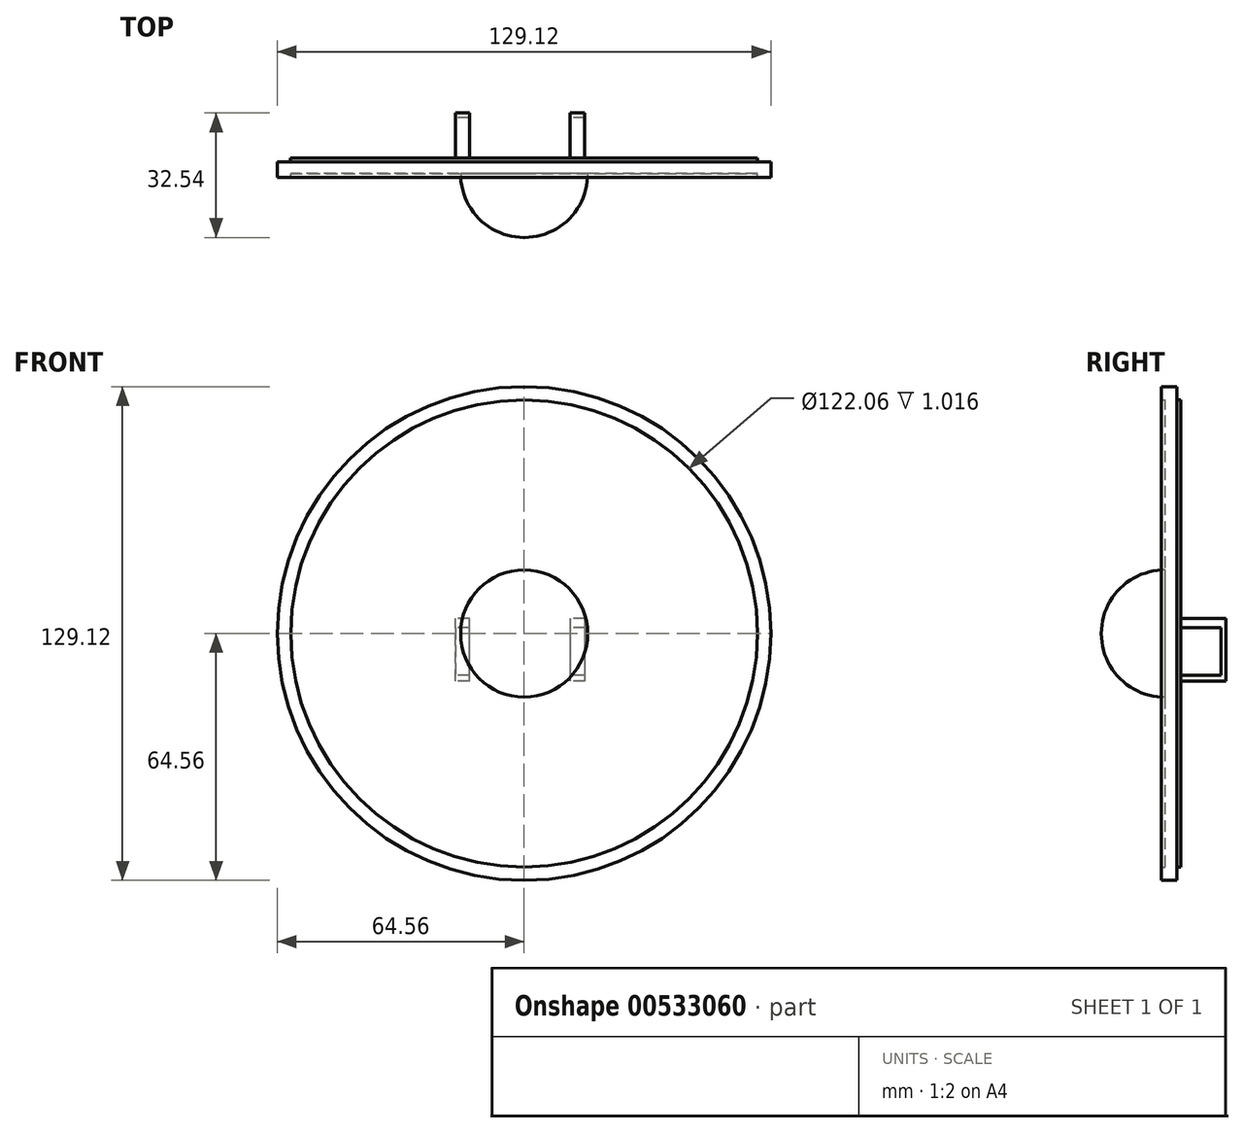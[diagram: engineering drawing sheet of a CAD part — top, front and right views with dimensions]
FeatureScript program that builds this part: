
annotation { "Feature Type Name" : "Feature", "Feature Type Description" : "" }
export const myFeature = defineFeature(function(context is Context, id is Id, definition is map)
    precondition{}
    {
        {
            var Q0;
            Q0=qCreatedBy(makeId("Front.planeOp"),FACE);
            var sketch = newSketch(context, id + "F0", { "sketchPlane" : qUnion([Q0])});
            skCircle(sketch, "E0", {"center": v(0, 0) * mm, "radius": 64.56 * mm});
            skSolve(sketch);
        }
        {
            var Q0;
            Q0=makeQuery(id+"F0.imprint","IMPRINT",FACE,{"disambiguationData":[TD([[makeQuery(id+"F0.imprint","IMPRINT",EDGE,{"derivedFrom":sQuery(id+"F0.wireOp",EDGE,"E0")}),1.0]])]});
            extrude(context, id + "F1", {"entities" : qUnion([Q0]), "endBound" : BoundingType.SYMMETRIC, "depth" : 3.05 * mm, "offsetDistance" : 25.4 * mm});
        }
        {
            var Q0;
            Q0=makeQuery(id+"F1.opExtrude","CAP_FACE",FACE,{"disambiguationData":[OSD([sQuery(id+"F0.wireOp",EDGE,"E0")])],"isStart":false});
            var sketch = newSketch(context, id + "F2", { "sketchPlane" : qUnion([Q0])});
            skCircle(sketch, "E1", {"center": v(0, 0) * mm, "radius": 61.03 * mm});
            skSolve(sketch);
        }
        {
            var Q0;
            Q0=makeQuery(id+"F2.imprint","IMPRINT",FACE,{"disambiguationData":[TD([[makeQuery(id+"F2.imprint","IMPRINT",EDGE,{"derivedFrom":sQuery(id+"F2.wireOp",EDGE,"E1")}),-1.0]])]});
            extrude(context, id + "F3", {"entities" : qUnion([Q0]), "operationType" : NewBodyOperationType.ADD, "depth" : 1.02 * mm, "offsetDistance" : 25.4 * mm});
        }
        {
            var Q0;
            Q0=makeQuery(id+"F1.opExtrude","CAP_FACE",FACE,{"disambiguationData":[OSD([sQuery(id+"F0.wireOp",EDGE,"E0")])],"isStart":false});
            var sketch = newSketch(context, id + "F4", { "sketchPlane" : qUnion([Q0])});
            skCircle(sketch, "E2", {"center": v(0, 0) * mm, "radius": 16.62 * mm});
            skSolve(sketch);
        }
        {
            var Q0;
            Q0=makeQuery(id+"F4.imprint","IMPRINT",FACE,{"disambiguationData":[TD([[makeQuery(id+"F4.imprint","IMPRINT",EDGE,{"derivedFrom":sQuery(id+"F4.wireOp",EDGE,"E2")}),1.0]])]});
            extrude(context, id + "F5", {"entities" : qUnion([Q0]), "operationType" : NewBodyOperationType.ADD, "depth" : 16.76 * mm, "offsetDistance" : 25.4 * mm});
        }
        {
            var Q0;
            Q0=makeQuery(id+"F5.opExtrude","CAP_EDGE",EDGE,{"disambiguationData":[OSD([sQuery(id+"F4.wireOp",EDGE,"E2")])],"isStart":false});
            fillet(context, id + "F6", {"entities" : qUnion([Q0]), "radius" : 16.56 * mm, "tangentPropagation" : true, "allowEdgeOverflow" : false});
        }
        {
            var Q0;
            Q0=makeQuery(id+"F1.opExtrude","CAP_FACE",FACE,{"disambiguationData":[OSD([sQuery(id+"F0.wireOp",EDGE,"E0")])],"isStart":true});
            var sketch = newSketch(context, id + "F7", { "sketchPlane" : qUnion([Q0])});
            skCircle(sketch, "E3", {"center": v(0, 0) * mm, "radius": 61.09 * mm});
            skSolve(sketch);
        }
        {
            var Q0;
            Q0 = qSketchRegion(id + "F7", true);
            extrude(context, id + "F8", {"entities" : qUnion([Q0]), "operationType" : NewBodyOperationType.ADD, "depth" : 1.02 * mm, "offsetDistance" : 25.4 * mm});
        }
        {
            var Q0;
            Q0=makeQuery(id+"F1.opExtrude","CAP_FACE",FACE,{"disambiguationData":[OSD([sQuery(id+"F0.wireOp",EDGE,"E0")])],"isStart":false});
            var sketch = newSketch(context, id + "F9", { "sketchPlane" : qUnion([Q0])});
            skLineSegment(sketch, "E4", {"start": v(-51.1, 33.39) * mm, "end": v(-51.1, -33.39) * mm});
            skLineSegment(sketch, "E5", {"start": v(-39.3, 46.7) * mm, "end": v(-39.3, -46.7) * mm});
            skLineSegment(sketch, "E6", {"start": v(-24.4, -55.94) * mm, "end": v(-24.4, 55.94) * mm});
            skLineSegment(sketch, "E7", {"start": v(-11.26, 59.99) * mm, "end": v(-11.26, 12.23) * mm});
            skLineSegment(sketch, "E8", {"start": v(-10.94, -12.5) * mm, "end": v(-10.94, -60.04) * mm});
            skLineSegment(sketch, "E9", {"start": v(3.47, -16.25) * mm, "end": v(3.47, -60.93) * mm});
            skLineSegment(sketch, "E10", {"start": v(3.1, 16.33) * mm, "end": v(3.1, 60.95) * mm});
            skLineSegment(sketch, "E11", {"start": v(17.62, 58.43) * mm, "end": v(17.62, -58.43) * mm});
            skLineSegment(sketch, "E12", {"start": v(32.37, -51.74) * mm, "end": v(32.37, 51.74) * mm});
            skLineSegment(sketch, "E13", {"start": v(48.38, -37.2) * mm, "end": v(48.38, 37.2) * mm});
            skSolve(sketch);
        }
        {
            var Q0;
            Q0=sQuery(id+"F9.wireOp",EDGE,"E4");
            var Q1;
            Q1=sQuery(id+"F9.wireOp",EDGE,"E5");
            var Q2;
            Q2=sQuery(id+"F9.wireOp",EDGE,"E6");
            var Q3;
            Q3=sQuery(id+"F9.wireOp",EDGE,"E7");
            var Q4;
            Q4=sQuery(id+"F9.wireOp",EDGE,"E8");
            var Q5;
            Q5=sQuery(id+"F9.wireOp",EDGE,"E10");
            var Q6;
            Q6=sQuery(id+"F9.wireOp",EDGE,"E9");
            var Q7;
            Q7=sQuery(id+"F9.wireOp",EDGE,"E11");
            var Q8;
            Q8=sQuery(id+"F9.wireOp",EDGE,"E12");
            var Q9;
            Q9=sQuery(id+"F9.wireOp",EDGE,"E13");
            extrude(context, id + "F10", {"bodyType" : ToolBodyType.SURFACE, "operationType" : NewBodyOperationType.ADD, "surfaceEntities" : qUnion([Q0, Q1, Q2, Q3, Q4, Q5, Q6, Q7, Q8, Q9]), "depth" : 0.03 * mm, "offsetDistance" : 25.4 * mm});
        }
        {
            var Q0;
            Q0=makeQuery(id+"F8.opExtrude","CAP_FACE",FACE,{"disambiguationData":[OSD([sQuery(id+"F7.wireOp",EDGE,"E3")])],"isStart":false});
            var sketch = newSketch(context, id + "F11", { "sketchPlane" : qUnion([Q0])});
            skLineSegment(sketch, "E14", {"start": v(-48.49, 37.16) * mm, "end": v(-48.49, -37.16) * mm});
            skLineSegment(sketch, "E15", {"start": v(-32.33, -51.83) * mm, "end": v(-32.33, 51.83) * mm});
            skLineSegment(sketch, "E16", {"start": v(-17.66, 58.48) * mm, "end": v(-17.66, -58.48) * mm});
            skLineSegment(sketch, "E17", {"start": v(-3.66, -60.98) * mm, "end": v(-3.66, 60.98) * mm});
            skLineSegment(sketch, "E18", {"start": v(11.21, 60.05) * mm, "end": v(11.21, -60.05) * mm});
            skLineSegment(sketch, "E19", {"start": v(24.29, -56.05) * mm, "end": v(24.29, 56.05) * mm});
            skLineSegment(sketch, "E20", {"start": v(39.02, 47) * mm, "end": v(39.02, -47) * mm});
            skLineSegment(sketch, "E21", {"start": v(51.06, -33.53) * mm, "end": v(51.06, 33.53) * mm});
            skSolve(sketch);
        }
        {
            var Q0;
            Q0=sQuery(id+"F11.wireOp",EDGE,"E14");
            var Q1;
            Q1=sQuery(id+"F11.wireOp",EDGE,"E15");
            var Q2;
            Q2=sQuery(id+"F11.wireOp",EDGE,"E16");
            var Q3;
            Q3=sQuery(id+"F11.wireOp",EDGE,"E17");
            var Q4;
            Q4=sQuery(id+"F11.wireOp",EDGE,"E18");
            var Q5;
            Q5=sQuery(id+"F11.wireOp",EDGE,"E19");
            var Q6;
            Q6=sQuery(id+"F11.wireOp",EDGE,"E20");
            var Q7;
            Q7=sQuery(id+"F11.wireOp",EDGE,"E21");
            extrude(context, id + "F12", {"bodyType" : ToolBodyType.SURFACE, "surfaceEntities" : qUnion([Q0, Q1, Q2, Q3, Q4, Q5, Q6, Q7]), "depth" : 0.03 * mm, "offsetDistance" : 25.4 * mm});
        }
        {
            var Q0;
            Q0=makeQuery(id+"F8.opExtrude","CAP_FACE",FACE,{"disambiguationData":[OSD([sQuery(id+"F7.wireOp",EDGE,"E3")])],"isStart":false});
            var sketch = newSketch(context, id + "F13", { "sketchPlane" : qUnion([Q0])});
            skLineSegment(sketch, "E22.bottom", {"start": v(-15.85, 3.97) * mm, "end": v(-11.98, 3.97) * mm});
            skLineSegment(sketch, "E22.top", {"start": v(-15.85, -12.38) * mm, "end": v(-11.98, -12.38) * mm});
            skLineSegment(sketch, "E22.left", {"start": v(-15.85, 3.97) * mm, "end": v(-15.85, -12.38) * mm});
            skLineSegment(sketch, "E22.right", {"start": v(-11.98, 3.97) * mm, "end": v(-11.98, -12.38) * mm});
            skLineSegment(sketch, "E23.bottom", {"start": v(14.3, -12.38) * mm, "end": v(17.94, -12.38) * mm});
            skLineSegment(sketch, "E23.top", {"start": v(14.3, 3.97) * mm, "end": v(17.94, 3.97) * mm});
            skLineSegment(sketch, "E23.left", {"start": v(14.3, -12.38) * mm, "end": v(14.3, 3.97) * mm});
            skLineSegment(sketch, "E23.right", {"start": v(17.94, -12.38) * mm, "end": v(17.94, 3.97) * mm});
            skSolve(sketch);
        }
        {
            var Q0;
            Q0=makeQuery(id+"F13.imprint","IMPRINT",FACE,{"disambiguationData":[TD([[makeQuery(id+"F13.imprint","IMPRINT",EDGE,{"derivedFrom":sQuery(id+"F13.wireOp",EDGE,"E22.bottom")}),-1.0]])]});
            var Q1;
            Q1=makeQuery(id+"F13.imprint","IMPRINT",FACE,{"disambiguationData":[TD([[makeQuery(id+"F13.imprint","IMPRINT",EDGE,{"derivedFrom":sQuery(id+"F13.wireOp",EDGE,"E23.bottom")}),1.0]])]});
            extrude(context, id + "F14", {"entities" : qUnion([Q0, Q1]), "operationType" : NewBodyOperationType.ADD, "depth" : 11.7 * mm, "offsetDistance" : 25.4 * mm});
        }
        {
            var Q0;
            Q0=makeQuery(id+"F14.opExtrude","SWEPT_FACE",FACE,{"disambiguationData":[OSD([sQuery(id+"F13.wireOp",EDGE,"E23.right")])]});
            var sketch = newSketch(context, id + "F15", { "sketchPlane" : qUnion([Q0])});
            skLineSegment(sketch, "E24", {"start": v(-2.54, 1.5) * mm, "end": v(-13, 1.5) * mm});
            skLineSegment(sketch, "E25", {"start": v(-13, 1.5) * mm, "end": v(-13, -10.94) * mm});
            skLineSegment(sketch, "E26", {"start": v(-13, -10.94) * mm, "end": v(-2.54, -10.94) * mm});
            skLineSegment(sketch, "E27", {"start": v(-2.54, -10.94) * mm, "end": v(-2.54, 1.5) * mm});
            skSolve(sketch);
        }
        {
            var Q0;
            Q0=makeQuery(id+"F15.imprint","IMPRINT",FACE,{"disambiguationData":[TD([[makeQuery(id+"F15.imprint","IMPRINT",EDGE,{"derivedFrom":sQuery(id+"F15.wireOp",EDGE,"E24")}),1.0]])]});
            extrude(context, id + "F16", {"entities" : qUnion([Q0]), "operationType" : NewBodyOperationType.REMOVE, "oppositeDirection" : true, "depth" : 37.62 * mm, "offsetDistance" : 25.4 * mm});
        }
    });
